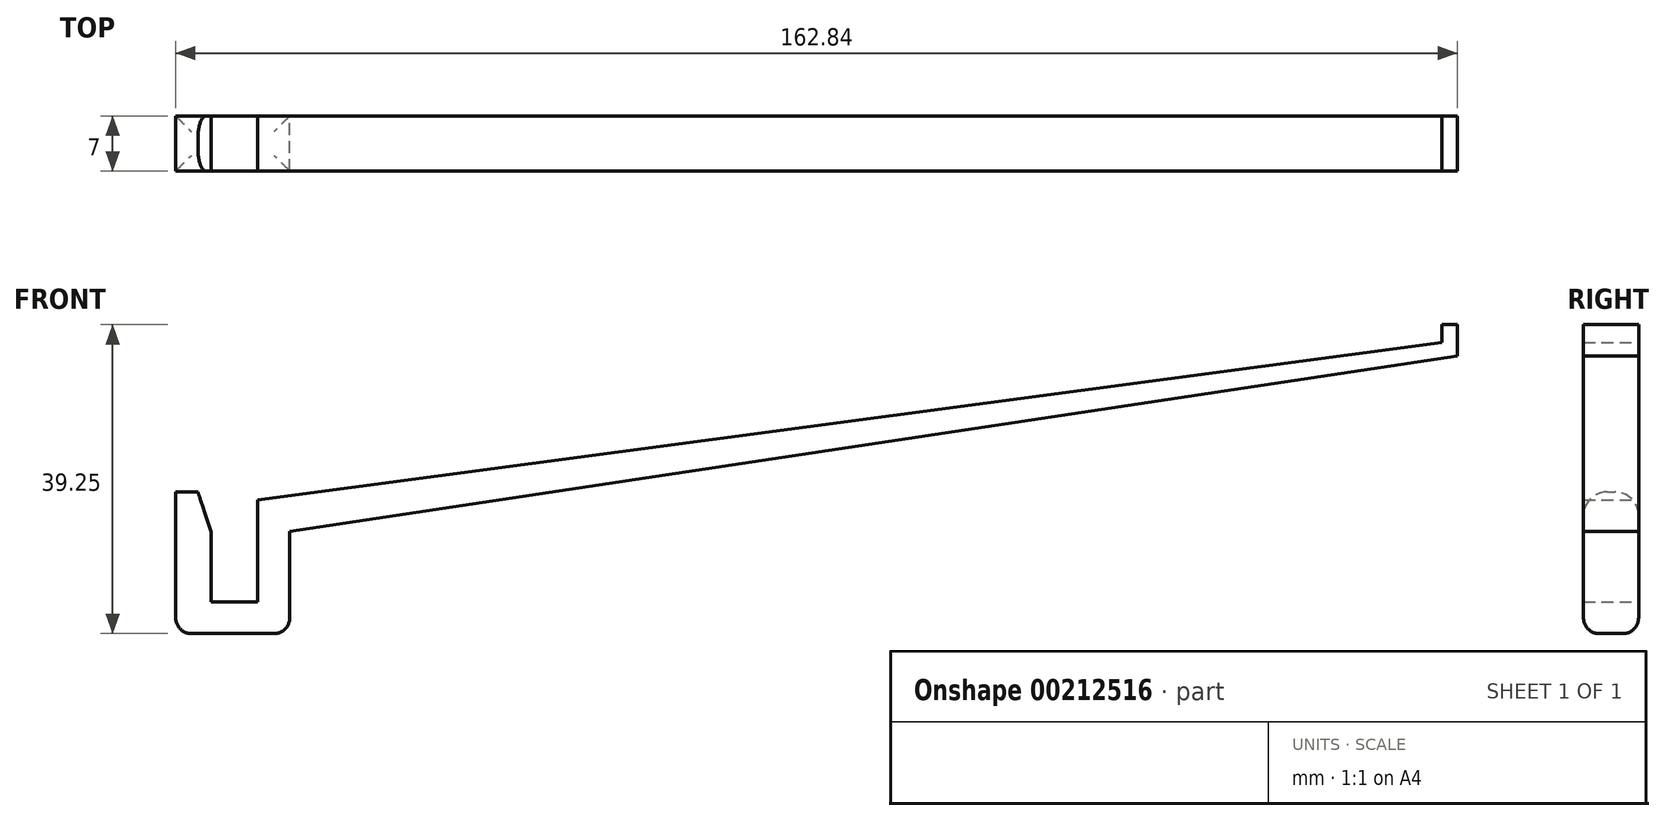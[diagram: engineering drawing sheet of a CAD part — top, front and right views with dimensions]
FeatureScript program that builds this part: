
annotation { "Feature Type Name" : "Feature", "Feature Type Description" : "" }
export const myFeature = defineFeature(function(context is Context, id is Id, definition is map)
    precondition{}
    {
        {
            var Q0;
            Q0=qCreatedBy(makeId("Front.planeOp"),FACE);
            var sketch = newSketch(context, id + "F0", { "sketchPlane" : qUnion([Q0])});
            skLineSegment(sketch, "E0", {"start": v(-33.33, -11.46) * mm, "end": v(-33.33, -2.57) * mm});
            skLineSegment(sketch, "E1", {"start": v(-37.83, -2.46) * mm, "end": v(-37.83, -15.46) * mm});
            skLineSegment(sketch, "E2", {"start": v(-37.83, -15.46) * mm, "end": v(-23.33, -15.46) * mm});
            skLineSegment(sketch, "E3", {"start": v(-23.33, -15.46) * mm, "end": v(-23.33, -6.46) * mm});
            skLineSegment(sketch, "E4", {"start": v(-27.43, -2.46) * mm, "end": v(-27.43, -11.46) * mm});
            skLineSegment(sketch, "E5", {"start": v(-27.43, -11.46) * mm, "end": v(-33.33, -11.46) * mm});
            skLineSegment(sketch, "E6", {"start": v(-36.68, 2.54) * mm, "end": v(-35, 2.54) * mm});
            skLineSegment(sketch, "E7", {"start": v(-37.83, -2.46) * mm, "end": v(-37.83, 2.54) * mm});
            skLineSegment(sketch, "E8", {"start": v(-36.68, 2.54) * mm, "end": v(-37.83, 2.54) * mm});
            skLineSegment(sketch, "E9", {"start": v(-27.43, -2.46) * mm, "end": v(-27.43, 1.54) * mm});
            skLineSegment(sketch, "E10", {"start": v(-27.43, 1.54) * mm, "end": v(123.01, 21.53) * mm});
            skLineSegment(sketch, "E11", {"start": v(125.01, 21.8) * mm, "end": v(125.01, 19.8) * mm});
            skLineSegment(sketch, "E12", {"start": v(-23.33, -6.46) * mm, "end": v(-23.33, -2.46) * mm});
            skLineSegment(sketch, "E13", {"start": v(125.01, 19.8) * mm, "end": v(-23.33, -2.46) * mm});
            skLineSegment(sketch, "E14", {"start": v(125.01, 21.8) * mm, "end": v(125.01, 23.8) * mm});
            skLineSegment(sketch, "E15", {"start": v(125.01, 23.8) * mm, "end": v(123.01, 23.8) * mm});
            skLineSegment(sketch, "E16", {"start": v(123.01, 23.8) * mm, "end": v(123.01, 21.53) * mm});
            skLineSegment(sketch, "E17", {"start": v(-35, 2.54) * mm, "end": v(-33.33, -2.57) * mm});
            skPoint(sketch, "E18.orphan", {"position": v(-33.33, 2.54) * mm});
            skSolve(sketch);
        }
        {
            var Q0;
            Q0=makeQuery(id+"F0.imprint","IMPRINT",FACE,{"disambiguationData":[TD([[makeQuery(id+"F0.imprint","IMPRINT",EDGE,{"derivedFrom":sQuery(id+"F0.wireOp",EDGE,"E0")}),1.0]])]});
            extrude(context, id + "F1", {"entities" : qUnion([Q0]), "endBound" : BoundingType.SYMMETRIC, "depth" : 7 * mm});
        }
        {
            var Q0;
            Q0=makeQuery(id+"F1.opExtrude","CAP_EDGE",EDGE,{"disambiguationData":[OSD([sQuery(id+"F0.wireOp",EDGE,"E6"),sQuery(id+"F0.wireOp",EDGE,"E8")])],"isStart":true});
            var Q1;
            Q1=makeQuery(id+"F1.opExtrude","CAP_EDGE",EDGE,{"disambiguationData":[OSD([sQuery(id+"F0.wireOp",EDGE,"E6"),sQuery(id+"F0.wireOp",EDGE,"E8")])],"isStart":false});
            fillet(context, id + "F2", {"entities" : qUnion([Q0, Q1]), "radius" : 3 * mm, "tangentPropagation" : true, "allowEdgeOverflow" : false});
        }
        {
            var Q0;
            Q0=makeQuery(id+"F1.opExtrude","SWEPT_FACE",FACE,{"disambiguationData":[OSD([sQuery(id+"F0.wireOp",EDGE,"E2")])]});
            fillet(context, id + "F3", {"entities" : qUnion([Q0]), "radius" : 2 * mm, "tangentPropagation" : true, "allowEdgeOverflow" : false});
        }
    });
